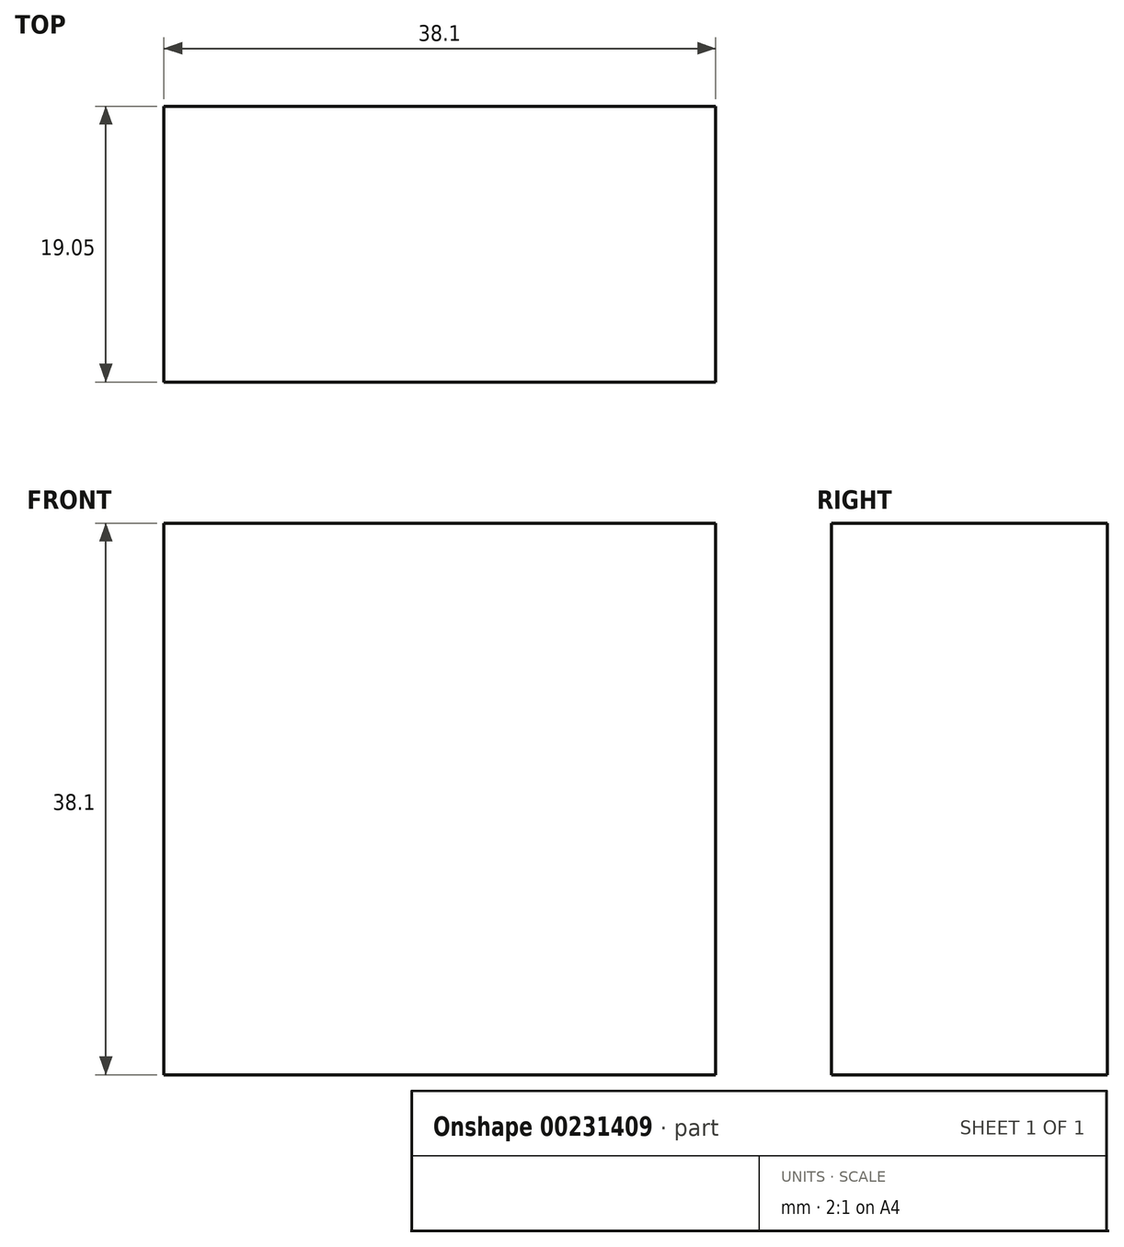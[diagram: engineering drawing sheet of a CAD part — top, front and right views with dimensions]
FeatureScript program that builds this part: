
annotation { "Feature Type Name" : "Feature", "Feature Type Description" : "" }
export const myFeature = defineFeature(function(context is Context, id is Id, definition is map)
    precondition{}
    {
        {
            var Q0;
            Q0=qCreatedBy(makeId("Front.planeOp"),FACE);
            var sketch = newSketch(context, id + "F0", { "sketchPlane" : qUnion([Q0])});
            skLineSegment(sketch, "E0.bottom", {"start": v(-61.11, 44.64) * mm, "end": v(-23.01, 44.64) * mm});
            skLineSegment(sketch, "E0.top", {"start": v(-61.11, 6.54) * mm, "end": v(-23.01, 6.54) * mm});
            skLineSegment(sketch, "E0.left", {"start": v(-61.11, 44.64) * mm, "end": v(-61.11, 6.54) * mm});
            skLineSegment(sketch, "E0.right", {"start": v(-23.01, 44.64) * mm, "end": v(-23.01, 6.54) * mm});
            skSolve(sketch);
        }
        {
            var Q0;
            Q0 = qSketchRegion(id + "F0", true);
            extrude(context, id + "F1", {"entities" : qUnion([Q0]), "depth" : 19.05 * mm});
        }
    });
